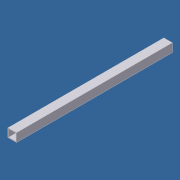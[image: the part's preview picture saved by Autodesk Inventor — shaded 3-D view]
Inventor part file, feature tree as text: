
AUTODESK INVENTOR PART (.ipt)
format: ipt  version: 2012 (Build 160160000, 160)  size: 70,144 bytes
history: native  units: in
note: dims shown in document units (in); Inventor stores cm internally (conversion verified against a paired STEP export)
features: extrude x1, sketch x1
ambient origin geometry x8: Origin, YZ Plane, XZ Plane, XY Plane, X Axis, Y Axis, Z Axis, Center Point
bodies: Solid1 (feature_tree)
feature tree (2):
  extrude  "Extrusion1"  Depth=1.75in
  sketch  "Sketch1"  dims[d0=0.125in d1=1.75in d2=32.0in d3=0.0in]
